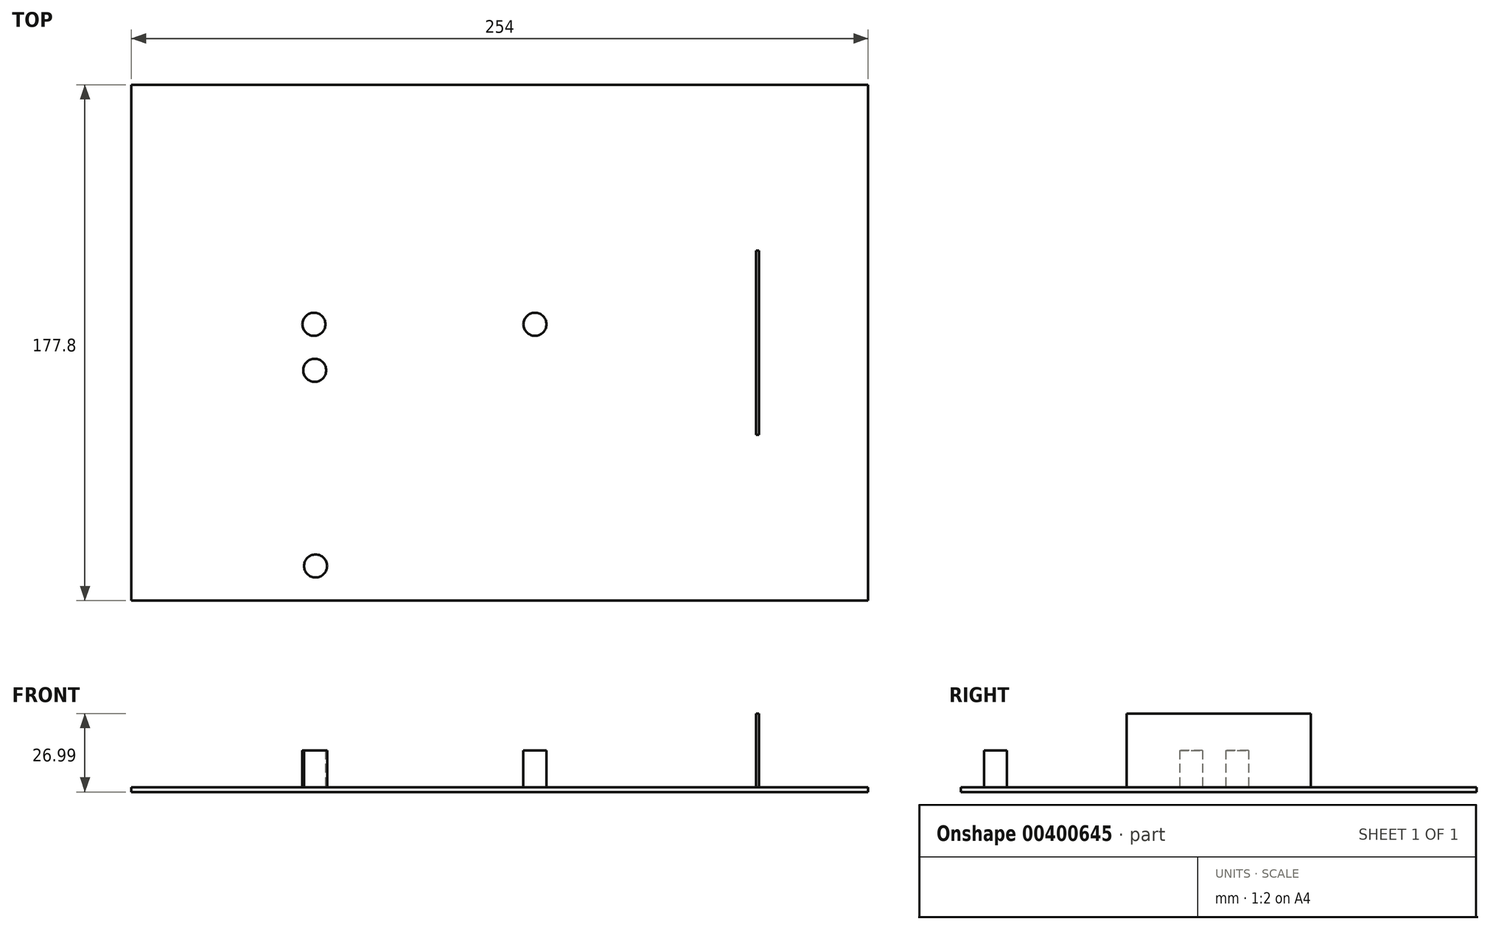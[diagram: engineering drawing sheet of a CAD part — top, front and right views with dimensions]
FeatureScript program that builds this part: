
annotation { "Feature Type Name" : "Feature", "Feature Type Description" : "" }
export const myFeature = defineFeature(function(context is Context, id is Id, definition is map)
    precondition{}
    {
        {
            var Q0;
            Q0=qCreatedBy(makeId("Top.planeOp"),FACE);
            var sketch = newSketch(context, id + "F0", { "sketchPlane" : qUnion([Q0])});
            skLineSegment(sketch, "E0.bottom", {"start": v(-97.8, 14.71) * mm, "end": v(156.2, 14.71) * mm});
            skLineSegment(sketch, "E0.top", {"start": v(-97.8, -163.09) * mm, "end": v(156.2, -163.09) * mm});
            skLineSegment(sketch, "E0.left", {"start": v(-97.8, 14.71) * mm, "end": v(-97.8, -163.09) * mm});
            skLineSegment(sketch, "E0.right", {"start": v(156.2, 14.71) * mm, "end": v(156.2, -163.09) * mm});
            skSolve(sketch);
        }
        {
            var Q0;
            Q0 = qSketchRegion(id + "F0", true);
            extrude(context, id + "F1", {"entities" : qUnion([Q0]), "depth" : 1.59 * mm});
        }
        {
            var Q0;
            Q0=makeQuery(id+"F1.opExtrude","CAP_FACE",FACE,{"disambiguationData":[OSD([sQuery(id+"F0.wireOp",EDGE,"E0.bottom"),sQuery(id+"F0.wireOp",EDGE,"E0.top"),sQuery(id+"F0.wireOp",EDGE,"E0.left"),sQuery(id+"F0.wireOp",EDGE,"E0.right")])],"isStart":false});
            var sketch = newSketch(context, id + "F2", { "sketchPlane" : qUnion([Q0])});
            skLineSegment(sketch, "E1.bottom", {"start": v(117.53, -42.44) * mm, "end": v(118.59, -42.44) * mm});
            skLineSegment(sketch, "E1.top", {"start": v(117.53, -105.94) * mm, "end": v(118.59, -105.94) * mm});
            skLineSegment(sketch, "E1.left", {"start": v(117.53, -42.44) * mm, "end": v(117.53, -105.94) * mm});
            skLineSegment(sketch, "E1.right", {"start": v(118.59, -42.44) * mm, "end": v(118.59, -105.94) * mm});
            skSolve(sketch);
        }
        {
            var Q0;
            Q0=makeQuery(id+"F2.imprint","IMPRINT",FACE,{"disambiguationData":[TD([[makeQuery(id+"F2.imprint","IMPRINT",EDGE,{"derivedFrom":sQuery(id+"F2.wireOp",EDGE,"E1.bottom")}),-1.0]])]});
            extrude(context, id + "F3", {"entities" : qUnion([Q0]), "operationType" : NewBodyOperationType.ADD, "depth" : 25.4 * mm});
        }
        {
            var Q0;
            Q0=makeQuery(id+"F1.opExtrude","CAP_FACE",FACE,{"disambiguationData":[OSD([sQuery(id+"F0.wireOp",EDGE,"E0.bottom"),sQuery(id+"F0.wireOp",EDGE,"E0.top"),sQuery(id+"F0.wireOp",EDGE,"E0.left"),sQuery(id+"F0.wireOp",EDGE,"E0.right")])],"isStart":false});
            var sketch = newSketch(context, id + "F4", { "sketchPlane" : qUnion([Q0])});
            skCircle(sketch, "E2", {"center": v(-34.6, -83.71) * mm, "radius": 3.97 * mm});
            skCircle(sketch, "E3", {"center": v(-34.87, -67.84) * mm, "radius": 3.97 * mm});
            skSolve(sketch);
        }
        {
            var Q0;
            Q0 = qSketchRegion(id + "F4", true);
            extrude(context, id + "F5", {"entities" : qUnion([Q0]), "operationType" : NewBodyOperationType.ADD, "depth" : 12.7 * mm});
        }
        {
            var Q0;
            Q0=makeQuery(id+"F1.opExtrude","CAP_FACE",FACE,{"disambiguationData":[OSD([sQuery(id+"F0.wireOp",EDGE,"E0.bottom"),sQuery(id+"F0.wireOp",EDGE,"E0.top"),sQuery(id+"F0.wireOp",EDGE,"E0.left"),sQuery(id+"F0.wireOp",EDGE,"E0.right")])],"isStart":false});
            var sketch = newSketch(context, id + "F6", { "sketchPlane" : qUnion([Q0])});
            skCircle(sketch, "E4", {"center": v(41.33, -67.84) * mm, "radius": 3.97 * mm});
            skCircle(sketch, "E5", {"center": v(-34.3, -151.18) * mm, "radius": 3.97 * mm});
            skSolve(sketch);
        }
        {
            var Q0;
            Q0 = qSketchRegion(id + "F6", true);
            extrude(context, id + "F7", {"entities" : qUnion([Q0]), "operationType" : NewBodyOperationType.ADD, "depth" : 12.7 * mm});
        }
    });
